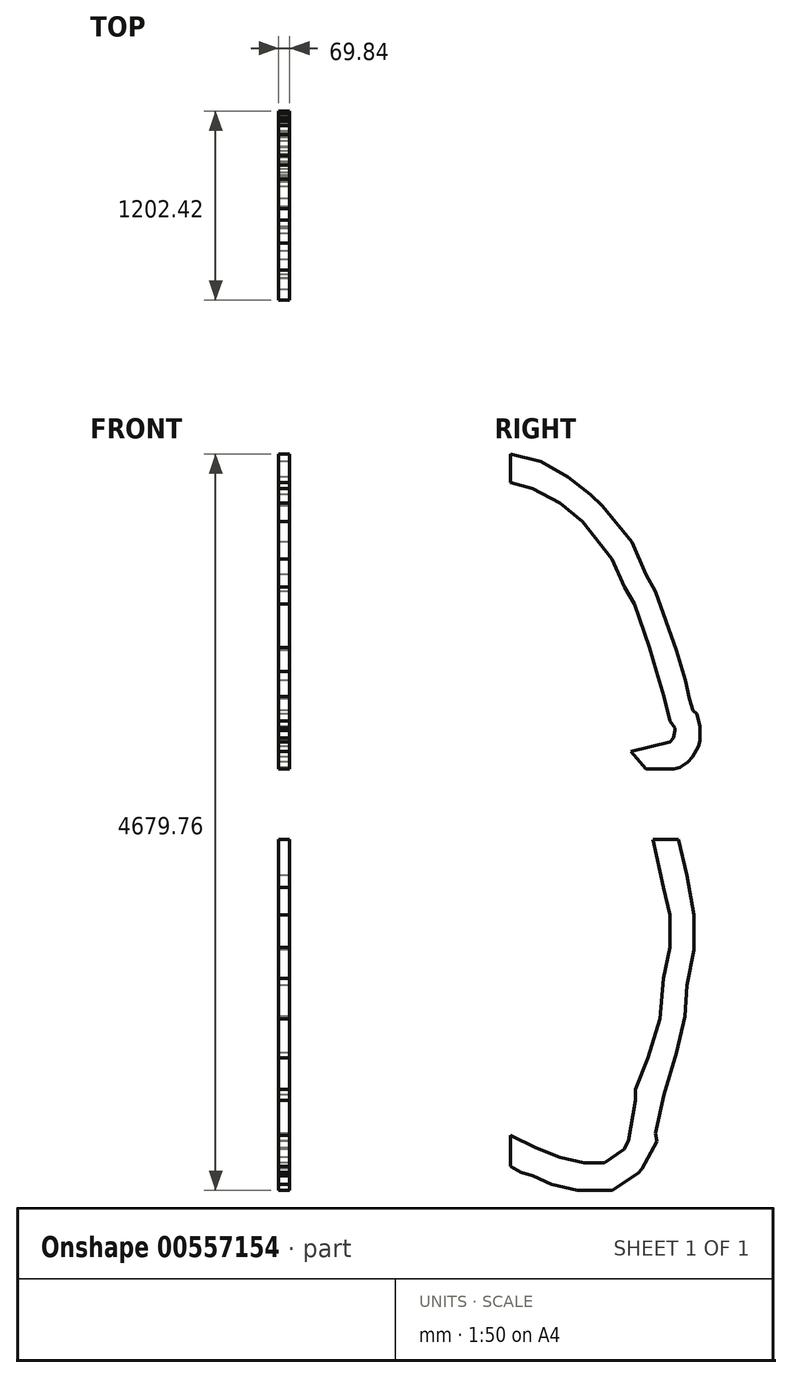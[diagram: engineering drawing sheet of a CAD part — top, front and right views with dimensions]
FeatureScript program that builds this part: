
annotation { "Feature Type Name" : "Feature", "Feature Type Description" : "" }
export const myFeature = defineFeature(function(context is Context, id is Id, definition is map)
    precondition{}
    {
        {
            var Q0;
            Q0=qCreatedBy(makeId("Right.planeOp"),FACE);
            var sketch = newSketch(context, id + "F0", { "sketchPlane" : qUnion([Q0])});
            skLineSegment(sketch, "E0", {"start": v(0, 153.9) * mm, "end": v(0, 350.34) * mm});
            skLineSegment(sketch, "E1", {"start": v(0, 350.34) * mm, "end": v(161.85, 271.2) * mm});
            skLineSegment(sketch, "E2", {"start": v(161.85, 271.2) * mm, "end": v(313.31, 211.55) * mm});
            skLineSegment(sketch, "E3", {"start": v(313.31, 211.55) * mm, "end": v(466.7, 176.33) * mm});
            skLineSegment(sketch, "E4", {"start": v(466.7, 176.33) * mm, "end": v(595.08, 176.33) * mm});
            skLineSegment(sketch, "E5", {"start": v(595.08, 176.33) * mm, "end": v(721.2, 261.54) * mm});
            skLineSegment(sketch, "E6", {"start": v(721.2, 261.54) * mm, "end": v(749.6, 317.2) * mm});
            skLineSegment(sketch, "E7", {"start": v(749.6, 317.2) * mm, "end": v(794.04, 572.65) * mm});
            skLineSegment(sketch, "E8", {"start": v(794.04, 572.65) * mm, "end": v(794.04, 643.7) * mm});
            skLineSegment(sketch, "E9", {"start": v(794.04, 643.7) * mm, "end": v(872.92, 843.95) * mm});
            skLineSegment(sketch, "E10", {"start": v(872.92, 843.95) * mm, "end": v(948.19, 1090.01) * mm});
            skLineSegment(sketch, "E11", {"start": v(948.19, 1090.01) * mm, "end": v(969.53, 1346.5) * mm});
            skLineSegment(sketch, "E12", {"start": v(969.53, 1346.5) * mm, "end": v(1010.57, 1544.16) * mm});
            skLineSegment(sketch, "E13", {"start": v(1010.57, 1544.16) * mm, "end": v(1010.57, 1750.33) * mm});
            skLineSegment(sketch, "E14", {"start": v(1010.57, 1750.33) * mm, "end": v(969.53, 1925.76) * mm});
            skLineSegment(sketch, "E15", {"start": v(969.53, 1925.76) * mm, "end": v(904.85, 2231.9) * mm});
            skLineSegment(sketch, "E16", {"start": v(904.85, 2231.9) * mm, "end": v(1064.65, 2231.9) * mm});
            skLineSegment(sketch, "E17", {"start": v(1064.65, 2231.9) * mm, "end": v(1118.64, 2000.66) * mm});
            skLineSegment(sketch, "E18", {"start": v(1118.64, 2000.66) * mm, "end": v(1165.23, 1750.33) * mm});
            skLineSegment(sketch, "E19", {"start": v(1165.23, 1750.33) * mm, "end": v(1165.23, 1529.52) * mm});
            skLineSegment(sketch, "E20", {"start": v(1165.23, 1529.52) * mm, "end": v(1121.18, 1302.69) * mm});
            skLineSegment(sketch, "E21", {"start": v(1121.18, 1302.69) * mm, "end": v(1106.08, 1107.3) * mm});
            skLineSegment(sketch, "E22", {"start": v(1106.08, 1107.3) * mm, "end": v(1054.45, 874.79) * mm});
            skLineSegment(sketch, "E23", {"start": v(1054.45, 874.79) * mm, "end": v(973.05, 608.69) * mm});
            skLineSegment(sketch, "E24", {"start": v(973.05, 608.69) * mm, "end": v(918.78, 362.7) * mm});
            skLineSegment(sketch, "E25", {"start": v(918.78, 362.7) * mm, "end": v(929.79, 313.02) * mm});
            skLineSegment(sketch, "E26", {"start": v(929.79, 313.02) * mm, "end": v(833.82, 138.87) * mm});
            skLineSegment(sketch, "E27", {"start": v(833.82, 138.87) * mm, "end": v(810.4, 113.5) * mm});
            skLineSegment(sketch, "E28", {"start": v(810.4, 113.5) * mm, "end": v(646.8, 0) * mm});
            skLineSegment(sketch, "E29", {"start": v(646.8, 0) * mm, "end": v(425.27, 0) * mm});
            skLineSegment(sketch, "E30", {"start": v(425.27, 0) * mm, "end": v(259.6, 41.02) * mm});
            skLineSegment(sketch, "E31", {"start": v(259.6, 41.02) * mm, "end": v(141.28, 94.3) * mm});
            skLineSegment(sketch, "E32", {"start": v(141.28, 94.3) * mm, "end": v(66.55, 117.16) * mm});
            skLineSegment(sketch, "E33", {"start": v(66.55, 117.16) * mm, "end": v(0, 153.9) * mm});
            skLineSegment(sketch, "E34", {"start": v(763.95, 2790.5) * mm, "end": v(1012.26, 2849.36) * mm});
            skLineSegment(sketch, "E35", {"start": v(1012.26, 2849.36) * mm, "end": v(1034.74, 2875.05) * mm});
            skLineSegment(sketch, "E36", {"start": v(1034.74, 2875.05) * mm, "end": v(1042.43, 2923.9) * mm});
            skLineSegment(sketch, "E37", {"start": v(1042.43, 2923.9) * mm, "end": v(1042.43, 2938.83) * mm});
            skLineSegment(sketch, "E38", {"start": v(1042.43, 2938.83) * mm, "end": v(1011.23, 2982.37) * mm});
            skLineSegment(sketch, "E39", {"start": v(1011.23, 2982.37) * mm, "end": v(975.38, 3137.98) * mm});
            skLineSegment(sketch, "E40", {"start": v(975.38, 3137.98) * mm, "end": v(925.58, 3295.7) * mm});
            skLineSegment(sketch, "E41", {"start": v(925.58, 3295.7) * mm, "end": v(882.4, 3450.1) * mm});
            skLineSegment(sketch, "E42", {"start": v(882.4, 3450.1) * mm, "end": v(785.43, 3725.62) * mm});
            skLineSegment(sketch, "E43", {"start": v(785.43, 3725.62) * mm, "end": v(721.52, 3833.48) * mm});
            skLineSegment(sketch, "E44", {"start": v(721.52, 3833.48) * mm, "end": v(644.62, 4012.24) * mm});
            skLineSegment(sketch, "E45", {"start": v(644.62, 4012.24) * mm, "end": v(455.33, 4250.22) * mm});
            skLineSegment(sketch, "E46", {"start": v(455.33, 4250.22) * mm, "end": v(313.88, 4368.42) * mm});
            skLineSegment(sketch, "E47", {"start": v(313.88, 4368.42) * mm, "end": v(137.68, 4459.8) * mm});
            skLineSegment(sketch, "E48", {"start": v(137.68, 4459.8) * mm, "end": v(0, 4496.06) * mm});
            skLineSegment(sketch, "E49", {"start": v(0, 4496.06) * mm, "end": v(0, 4679.76) * mm});
            skLineSegment(sketch, "E50", {"start": v(0, 4679.76) * mm, "end": v(192.8, 4631.26) * mm});
            skLineSegment(sketch, "E51", {"start": v(192.8, 4631.26) * mm, "end": v(364.74, 4532.06) * mm});
            skLineSegment(sketch, "E52", {"start": v(364.74, 4532.06) * mm, "end": v(508, 4422.4) * mm});
            skLineSegment(sketch, "E53", {"start": v(508, 4422.4) * mm, "end": v(583.71, 4348.7) * mm});
            skLineSegment(sketch, "E54", {"start": v(583.71, 4348.7) * mm, "end": v(769.58, 4118.2) * mm});
            skLineSegment(sketch, "E55", {"start": v(769.58, 4118.2) * mm, "end": v(859.91, 3914.4) * mm});
            skLineSegment(sketch, "E56", {"start": v(859.91, 3914.4) * mm, "end": v(918.89, 3805.3) * mm});
            skLineSegment(sketch, "E57", {"start": v(918.89, 3805.3) * mm, "end": v(1052.27, 3429.15) * mm});
            skLineSegment(sketch, "E58", {"start": v(1052.27, 3429.15) * mm, "end": v(1109.44, 3239.1) * mm});
            skLineSegment(sketch, "E59", {"start": v(1109.44, 3239.1) * mm, "end": v(1136.56, 3121.4) * mm});
            skLineSegment(sketch, "E60", {"start": v(1136.56, 3121.4) * mm, "end": v(1159.16, 3048.26) * mm});
            skLineSegment(sketch, "E61", {"start": v(1159.16, 3048.26) * mm, "end": v(1184.41, 3027.16) * mm});
            skLineSegment(sketch, "E62", {"start": v(1184.41, 3027.16) * mm, "end": v(1202.42, 2949.01) * mm});
            skLineSegment(sketch, "E63", {"start": v(1202.42, 2949.01) * mm, "end": v(1202.42, 2854.81) * mm});
            skLineSegment(sketch, "E64", {"start": v(1202.42, 2854.81) * mm, "end": v(1192.65, 2819.59) * mm});
            skLineSegment(sketch, "E65", {"start": v(1192.65, 2819.59) * mm, "end": v(1154.4, 2755.3) * mm});
            skLineSegment(sketch, "E66", {"start": v(1154.4, 2755.3) * mm, "end": v(1126.92, 2722.42) * mm});
            skLineSegment(sketch, "E67", {"start": v(1126.92, 2722.42) * mm, "end": v(1074.81, 2686.53) * mm});
            skLineSegment(sketch, "E68", {"start": v(1074.81, 2686.53) * mm, "end": v(1037.45, 2677.92) * mm});
            skLineSegment(sketch, "E69", {"start": v(1037.45, 2677.92) * mm, "end": v(860.78, 2677.92) * mm});
            skLineSegment(sketch, "E70", {"start": v(860.78, 2677.92) * mm, "end": v(763.95, 2790.5) * mm});
            skSolve(sketch);
        }
        {
            var Q0;
            Q0 = qSketchRegion(id + "F0", true);
            extrude(context, id + "F1", {"entities" : qUnion([Q0]), "depth" : 69.85 * mm, "offsetDistance" : 25.4 * mm, "symmetric" : true});
        }
    });
